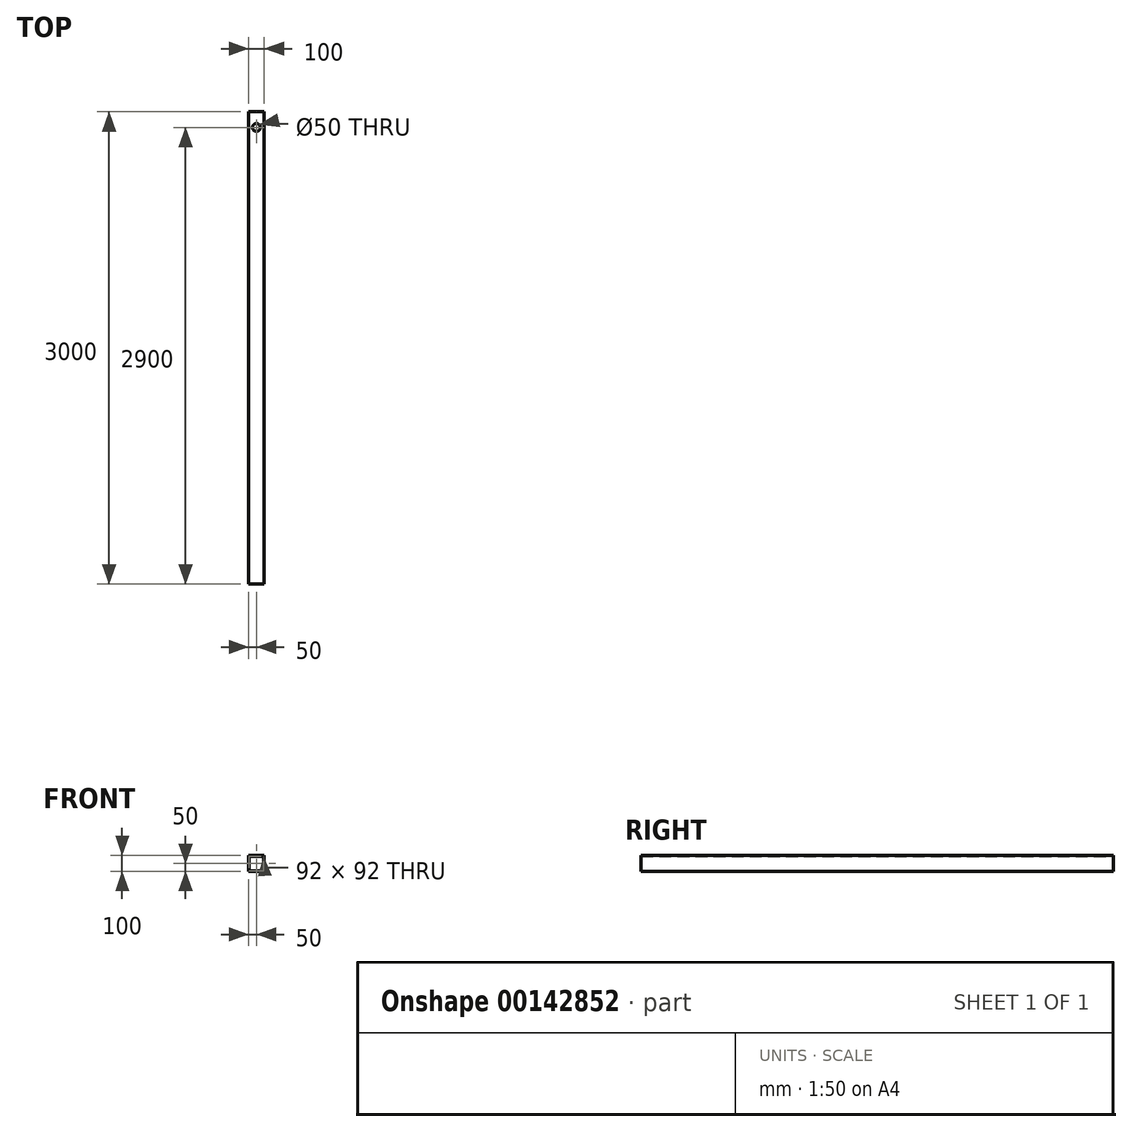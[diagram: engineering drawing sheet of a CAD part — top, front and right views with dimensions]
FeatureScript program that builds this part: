
annotation { "Feature Type Name" : "Feature", "Feature Type Description" : "" }
export const myFeature = defineFeature(function(context is Context, id is Id, definition is map)
    precondition{}
    {
        {
            var Q0;
            Q0=qCreatedBy(makeId("Front.planeOp"),FACE);
            var sketch = newSketch(context, id + "F0", { "sketchPlane" : qUnion([Q0])});
            skLineSegment(sketch, "E0.bottom", {"start": v(0, 0) * mm, "end": v(100, 0) * mm});
            skLineSegment(sketch, "E0.top", {"start": v(0, 100) * mm, "end": v(100, 100) * mm});
            skLineSegment(sketch, "E0.left", {"start": v(0, 0) * mm, "end": v(0, 100) * mm});
            skLineSegment(sketch, "E0.right", {"start": v(100, 0) * mm, "end": v(100, 100) * mm});
            skSolve(sketch);
        }
        {
            var Q0;
            Q0 = qSketchRegion(id + "F0", true);
            extrude(context, id + "F1", {"entities" : qUnion([Q0]), "depth" : 3000 * mm});
        }
        {
            var Q0;
            Q0=makeQuery(id+"F1.opExtrude","CAP_FACE",FACE,{"disambiguationData":[OSD([sQuery(id+"F0.wireOp",EDGE,"E0.bottom"),sQuery(id+"F0.wireOp",EDGE,"E0.top"),sQuery(id+"F0.wireOp",EDGE,"E0.left"),sQuery(id+"F0.wireOp",EDGE,"E0.right")])],"isStart":true});
            var sketch = newSketch(context, id + "F2", { "sketchPlane" : qUnion([Q0])});
            skLineSegment(sketch, "E1.bottom", {"start": v(-4, 96) * mm, "end": v(-96, 96) * mm});
            skLineSegment(sketch, "E1.top", {"start": v(-4, 4) * mm, "end": v(-96, 4) * mm});
            skLineSegment(sketch, "E1.left", {"start": v(-4, 96) * mm, "end": v(-4, 4) * mm});
            skLineSegment(sketch, "E1.right", {"start": v(-96, 96) * mm, "end": v(-96, 4) * mm});
            skPoint(sketch, "E1.middle", {"position": v(-50, 50) * mm});
            skSolve(sketch);
        }
        {
            var Q0;
            Q0 = qSketchRegion(id + "F2", true);
            extrude(context, id + "F3", {"entities" : qUnion([Q0]), "operationType" : NewBodyOperationType.REMOVE, "endBound" : BoundingType.THROUGH_ALL, "oppositeDirection" : true, "depth" : 25 * mm});
        }
        {
            var Q0;
            Q0=makeQuery(id+"F1.opExtrude","SWEPT_FACE",FACE,{"disambiguationData":[OSD([sQuery(id+"F0.wireOp",EDGE,"E0.top")])]});
            var sketch = newSketch(context, id + "F4", { "sketchPlane" : qUnion([Q0])});
            skPoint(sketch, "E2.endSnap0", {"position": v(50, 0) * mm});
            skCircle(sketch, "E3", {"center": v(50, -100) * mm, "radius": 25 * mm});
            skSolve(sketch);
        }
        {
            var Q0;
            Q0 = qSketchRegion(id + "F4", true);
            extrude(context, id + "F5", {"entities" : qUnion([Q0]), "operationType" : NewBodyOperationType.REMOVE, "endBound" : BoundingType.UP_TO_NEXT, "oppositeDirection" : true, "depth" : 25 * mm});
        }
    });
